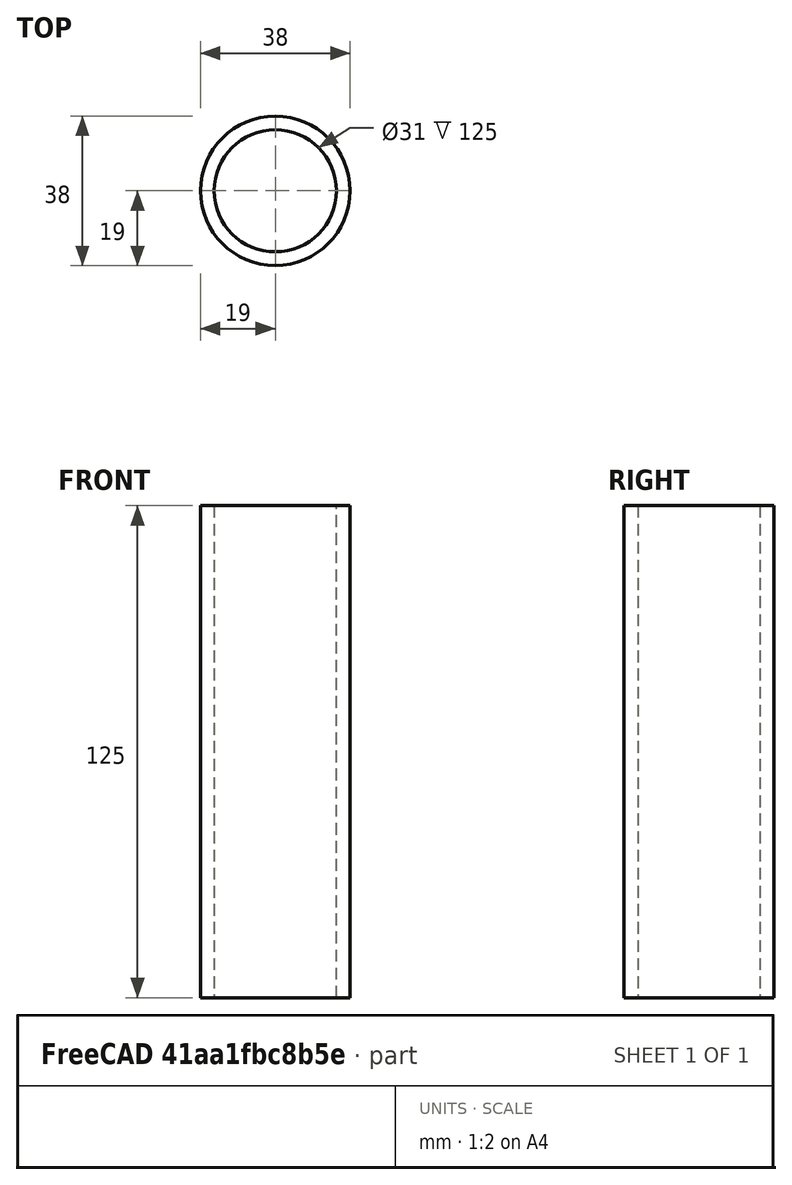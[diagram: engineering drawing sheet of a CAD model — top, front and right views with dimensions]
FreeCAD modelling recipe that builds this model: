
FCSTD DOCUMENT  (FreeCAD 0.21R33771 (Git))
Label: Case
License: All rights reserved
LicenseURL: http://en.wikipedia.org/wiki/All_rights_reserved
objects: Sketcher::SketchObject×1, PartDesign::Pad×1, PartDesign::Body×1
note: 4 computed .brp shape members not serialized (recipe doc carries the construction recipe); baked Part::Feature solids carry a one-line shape summary decoded from their .brp

FEATURE [Sketcher::SketchObject] Sketch
  FullyConstrained = true
  MapMode = 5
  Support = -> [XY_Plane]
  sketch-geometry (2):
    g0: Circle CenterX=0 CenterY=0 CenterZ=0 NormalX=0 NormalY=0 NormalZ=1 AngleXU=0 Radius=19
    g1: Circle CenterX=0 CenterY=0 CenterZ=0 NormalX=0 NormalY=0 NormalZ=1 AngleXU=0 Radius=15.5
  constraints (4):
    c: Coincident(g0,g-1)
    c: Coincident(g1,g0)
    c: Diameter(g1) = 31
    c: Diameter(g0) = 38
FEATURE [PartDesign::Pad] Pad
  Direction = (0,0,1)
  Length = 125
  Length2 = 10
  Profile = -> Sketch
  ReferenceAxis = -> Sketch [N_Axis]
  Type = 0
FEATURE [PartDesign::Body] Body  label="PVC"
  Group = -> [Sketch,Pad]
  Origin = -> Origin
  Tip = -> Pad
